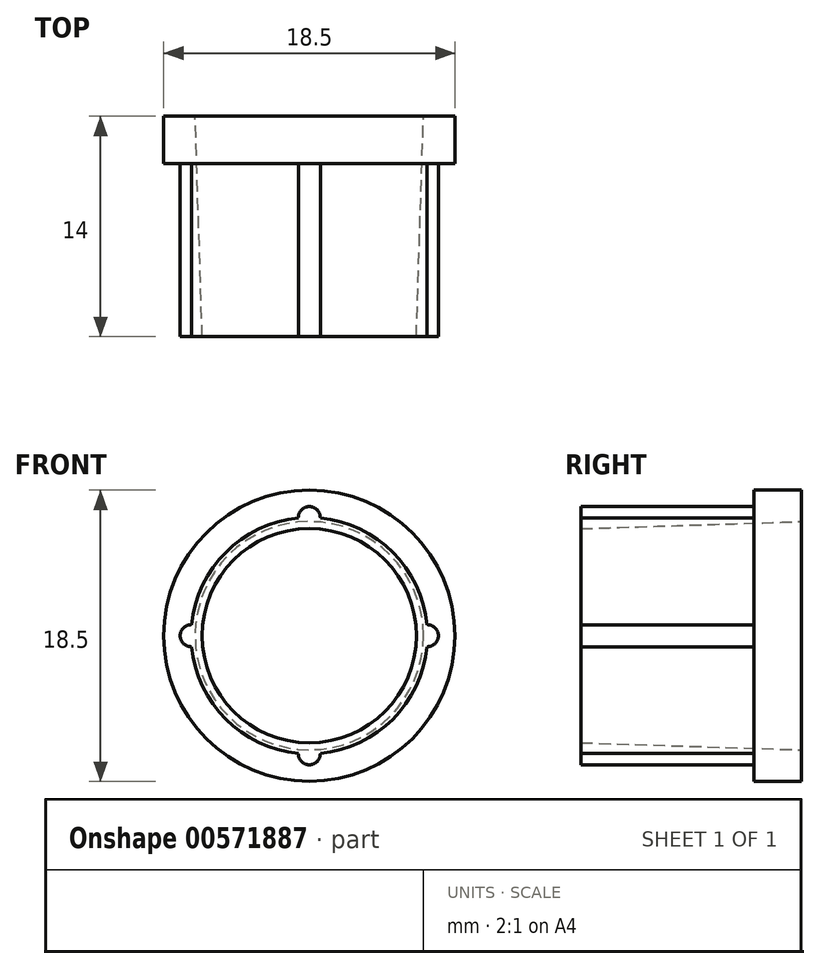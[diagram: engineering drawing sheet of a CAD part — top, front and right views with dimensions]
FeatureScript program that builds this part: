
annotation { "Feature Type Name" : "Feature", "Feature Type Description" : "" }
export const myFeature = defineFeature(function(context is Context, id is Id, definition is map)
    precondition{}
    {
        {
            var Q0;
            Q0=qCreatedBy(makeId("Top.planeOp"),FACE);
            var sketch = newSketch(context, id + "F0", { "sketchPlane" : qUnion([Q0])});
            skLineSegment(sketch, "E0", {"start": v(0, 0) * mm, "end": v(7.5, 0) * mm});
            skLineSegment(sketch, "E1", {"start": v(7.5, 0) * mm, "end": v(7.5, -11) * mm});
            skLineSegment(sketch, "E2", {"start": v(7.5, -11) * mm, "end": v(0, -11) * mm});
            skLineSegment(sketch, "E3", {"start": v(0, -11) * mm, "end": v(0, 0) * mm});
            skLineSegment(sketch, "E4", {"start": v(7.5, 0) * mm, "end": v(9.25, 0) * mm});
            skLineSegment(sketch, "E5", {"start": v(9.25, 0) * mm, "end": v(9.25, 3) * mm});
            skLineSegment(sketch, "E6", {"start": v(9.25, 3) * mm, "end": v(0, 3) * mm});
            skLineSegment(sketch, "E7", {"start": v(0, 3) * mm, "end": v(0, 0) * mm});
            skLineSegment(sketch, "E8", {"start": v(0, -11) * mm, "end": v(6.75, -11) * mm});
            skLineSegment(sketch, "E9", {"start": v(6.75, -11) * mm, "end": v(6.75, 3) * mm});
            skSolve(sketch);
        }
        {
            var Q0;
            {var subQ4=sQuery(id+"F0.wireOp",EDGE,"E4");Q0=makeQuery(id+"F0.imprint","IMPRINT",FACE,{"disambiguationData":[TD([[makeQuery(id+"F0.imprint","IMPRINT",EDGE,{"derivedFrom":subQ4}),1.0]])]});}
            var Q1;
            {var subQ0=sQuery(id+"F0.wireOp",EDGE,"E1");Q1=makeQuery(id+"F0.imprint","IMPRINT",FACE,{"disambiguationData":[TD([[makeQuery(id+"F0.imprint","IMPRINT",EDGE,{"derivedFrom":subQ0}),-1.0]])]});}
            var Q2;
            Q2=sQuery(id+"F0.wireOp",EDGE,"E3");
            revolve(context, id + "F1", {"entities" : qUnion([Q0, Q1]), "axis" : qUnion([Q2]), "revolveType" : RevolveType.FULL});
        }
        {
            var Q0;
            Q0=makeQuery(id+"F1.opRevolve","SWEPT_EDGE",EDGE,{"disambiguationData":[OSD([sQuery(id+"F0.wireOp",EDGE,"E6"),sQuery(id+"F0.wireOp",EDGE,"E9")])]});
            chamfer(context, id + "F2", {"entities" : qUnion([Q0]), "chamferType" : ChamferType.TWO_OFFSETS, "width1" : 0.5 * mm, "oppositeDirection" : false, "width2" : 15.5 * mm, "tangentPropagation" : true});
        }
        {
            var Q0;
            Q0=makeQuery(id+"F1.opRevolve","SWEPT_FACE",FACE,{"disambiguationData":[OSD([sQuery(id+"F0.wireOp",EDGE,"E4")])]});
            var sketch = newSketch(context, id + "F3", { "sketchPlane" : qUnion([Q0])});
            skCircle(sketch, "E10", {"center": v(0, 7.5) * mm, "radius": 0.7 * mm});
            skCircle(sketch, "E11", {"center": v(7.5, 0) * mm, "radius": 0.7 * mm});
            skCircle(sketch, "E12", {"center": v(0, -7.5) * mm, "radius": 0.7 * mm});
            skCircle(sketch, "E13", {"center": v(-7.5, 0) * mm, "radius": 0.7 * mm});
            skSolve(sketch);
        }
        {
            var Q0;
            {var subQ0=sQuery(id+"F3.wireOp",EDGE,"E10");var subQ1=makeQuery(id+"F1.opRevolve","SWEPT_EDGE",EDGE,{"disambiguationData":[OSD([sQuery(id+"F0.wireOp",EDGE,"E0"),sQuery(id+"F0.wireOp",EDGE,"E1"),sQuery(id+"F0.wireOp",EDGE,"E4")])]});var subQ2=makeQuery(id+"F3.imprint","INTERSECT",VERTEX,{"disambiguationData":[OD(0.0)],"derivedFrom":[subQ1,subQ0]});Q0=makeQuery(id+"F3.imprint","IMPRINT",FACE,{"disambiguationData":[TD([[makeQuery(id+"F3.imprint","IMPRINT",EDGE,{"disambiguationData":[TD([[subQ2,1.0]])],"derivedFrom":subQ0}),1.0]])]});}
            var Q1;
            {var subQ0=sQuery(id+"F3.wireOp",EDGE,"E13");var subQ1=makeQuery(id+"F1.opRevolve","SWEPT_EDGE",EDGE,{"disambiguationData":[OSD([sQuery(id+"F0.wireOp",EDGE,"E0"),sQuery(id+"F0.wireOp",EDGE,"E1"),sQuery(id+"F0.wireOp",EDGE,"E4")])]});var subQ2=makeQuery(id+"F3.imprint","INTERSECT",VERTEX,{"disambiguationData":[OD(0.0)],"derivedFrom":[subQ1,subQ0]});Q1=makeQuery(id+"F3.imprint","IMPRINT",FACE,{"disambiguationData":[TD([[makeQuery(id+"F3.imprint","IMPRINT",EDGE,{"disambiguationData":[TD([[subQ2,1.0]])],"derivedFrom":subQ0}),1.0]])]});}
            var Q2;
            {var subQ0=sQuery(id+"F3.wireOp",EDGE,"E12");var subQ1=makeQuery(id+"F1.opRevolve","SWEPT_EDGE",EDGE,{"disambiguationData":[OSD([sQuery(id+"F0.wireOp",EDGE,"E0"),sQuery(id+"F0.wireOp",EDGE,"E1"),sQuery(id+"F0.wireOp",EDGE,"E4")])]});var subQ2=makeQuery(id+"F3.imprint","INTERSECT",VERTEX,{"disambiguationData":[OD(0.0)],"derivedFrom":[subQ1,subQ0]});Q2=makeQuery(id+"F3.imprint","IMPRINT",FACE,{"disambiguationData":[TD([[makeQuery(id+"F3.imprint","IMPRINT",EDGE,{"disambiguationData":[TD([[subQ2,-1.0]])],"derivedFrom":subQ0}),1.0]])]});}
            var Q3;
            {var subQ0=sQuery(id+"F3.wireOp",EDGE,"E11");var subQ1=makeQuery(id+"F1.opRevolve","SWEPT_EDGE",EDGE,{"disambiguationData":[OSD([sQuery(id+"F0.wireOp",EDGE,"E0"),sQuery(id+"F0.wireOp",EDGE,"E1"),sQuery(id+"F0.wireOp",EDGE,"E4")])]});var subQ2=makeQuery(id+"F3.imprint","INTERSECT",VERTEX,{"disambiguationData":[OD(0.0)],"derivedFrom":[subQ1,subQ0]});Q3=makeQuery(id+"F3.imprint","IMPRINT",FACE,{"disambiguationData":[TD([[makeQuery(id+"F3.imprint","IMPRINT",EDGE,{"disambiguationData":[TD([[subQ2,-1.0]])],"derivedFrom":subQ0}),1.0]])]});}
            extrude(context, id + "F4", {"entities" : qUnion([Q0, Q1, Q2, Q3]), "operationType" : NewBodyOperationType.ADD, "depth" : 11 * mm, "offsetDistance" : 25 * mm});
        }
    });
